# Revit family: 872-00-002-DN80-900
name_source: partatom
category: Pipe Accessories
units: mm (PartAtom-declared; Revit-internal decimal feet)

## family parameters
Always vertical = Yes
Cut with Voids When Loaded = No
Part Type = Valve - Breaks Into
Round Connector Dimension = Use Diameter
Shared = No
Work Plane-Based = No

## types (13) — shared parameters
Body_wallthickness = 10 mm  [stored 0.0328084 ft]
DN080_PN25 = 872-0080-00-70900100100
DN100_PN25 = 872-0100-00-70900100100
DN150_PN25 = 872-0150-00-70900100100
DN200_PN25 = 872-0200-00-70100100000
DN250_PN25 = 872-0250-00-70100100000
DN300_PN25 = 872-0300-00-70100100000
DN350_PN25 = 872-0350-00-70100100000
DN400_PN25 = 872-0400-00-70100100000
DN450_PN25 = 872-0450-00-70100100000
DN500_PN25 = 872-0500-00-70100100000
DN600_PN25 = 872-0600-00-70100100000
DN800_PN25 = 872-0800-00-70100100000
DN900_PN25 = 872-0900-00-70100100000
Description_ = AVK NEEDLE VALVE
RF_Thick = 3 mm  [stored 0.00984252 ft]
Search_Table = 872-00-002-DN80-900
URL product pages = https://www.avkvalves.com

## per-type parameters (varying)
- DN0080_PN25: (A_ref+W)/2=303 mm; A=125 mm; A_ref=275 mm; B=117 mm; D=100 mm; DN=80 mm  [stored 0.262467 ft]; FOD=95 mm; FOD_ref=50 mm  [stored 0.164042 ft]; FOD_ref_2=32 mm  [stored 0.104987 ft]; Fillet_thickness=10 mm  [stored 0.0328084 ft]; Flange_thickness=19 mm  [stored 0.062336 ft]; Flange_thickness_ref=10 mm  [stored 0.0328084 ft]; Flange_thickness_ref_2=5 mm  [stored 0.0164042 ft]; H3=230 mm; H3_ref=195 mm; ID=40 mm  [stored 0.131234 ft]; ID_ref=70 mm  [stored 0.229659 ft]; ID_ref_2=35 mm  [stored 0.114829 ft]; ID_ref_3=105 mm; ID_ref_4=35 mm  [stored 0.114829 ft]; L=260 mm; L1=111 mm; L2=65 mm  [stored 0.213255 ft]; Rf_Dia=66 mm  [stored 0.216535 ft]; Ring_Dia=35 mm  [stored 0.114829 ft]; Ring_Dia_2=15 mm  [stored 0.0492126 ft]; W=330 mm
- DN0100_PN25: (A_ref+W)/2=339 mm; A=145 mm; A_ref=308 mm; B=117 mm; D=120 mm; DN=100 mm; FOD=100 mm; FOD_ref=60 mm  [stored 0.19685 ft]; FOD_ref_2=33 mm; Fillet_thickness=10 mm  [stored 0.0328084 ft]; Flange_thickness=19 mm  [stored 0.062336 ft]; Flange_thickness_ref=10 mm  [stored 0.0328084 ft]; Flange_thickness_ref_2=5 mm  [stored 0.0164042 ft]; H3=235 mm; H3_ref=200 mm; ID=50 mm  [stored 0.164042 ft]; ID_ref=70 mm  [stored 0.229659 ft]; ID_ref_2=35 mm  [stored 0.114829 ft]; ID_ref_3=105 mm; ID_ref_4=35 mm  [stored 0.114829 ft]; L=300 mm; L1=131 mm; L2=75 mm  [stored 0.246063 ft]; Rf_Dia=78 mm  [stored 0.255906 ft]; Ring_Dia=35 mm  [stored 0.114829 ft]; Ring_Dia_2=15 mm  [stored 0.0492126 ft]; W=370 mm
- DN0150_PN25: (A_ref+W)/2=403 mm; A=175 mm; A_ref=370 mm; B=150 mm; D=135 mm; DN=150 mm; FOD=130 mm; FOD_ref=85 mm; FOD_ref_2=43 mm  [stored 0.141076 ft]; Fillet_thickness=10 mm  [stored 0.0328084 ft]; Flange_thickness=19 mm  [stored 0.062336 ft]; Flange_thickness_ref=10 mm  [stored 0.0328084 ft]; Flange_thickness_ref_2=5 mm  [stored 0.0164042 ft]; H3=300 mm; H3_ref=265 mm; ID=75 mm  [stored 0.246063 ft]; ID_ref=70 mm  [stored 0.229659 ft]; ID_ref_2=35 mm  [stored 0.114829 ft]; ID_ref_3=105 mm; ID_ref_4=35 mm  [stored 0.114829 ft]; L=350 mm; L1=156 mm; L2=88 mm; Rf_Dia=106 mm; Ring_Dia=35 mm  [stored 0.114829 ft]; Ring_Dia_2=15 mm  [stored 0.0492126 ft]; W=435 mm
- DN0200_PN25: (A_ref+W)/2=480 mm; A=220 mm; A_ref=450 mm; B=150 mm; D=150 mm; DN=200 mm; FOD=170 mm; FOD_ref=110 mm; FOD_ref_2=57 mm; Fillet_thickness=20 mm  [stored 0.0656168 ft]; Flange_thickness=20 mm  [stored 0.0656168 ft]; Flange_thickness_ref=10 mm  [stored 0.0328084 ft]; Flange_thickness_ref_2=5 mm  [stored 0.0164042 ft]; H3=425 mm; H3_ref=380 mm; ID=100 mm; ID_ref=90 mm; ID_ref_2=45 mm  [stored 0.147638 ft]; ID_ref_3=135 mm; ID_ref_4=45 mm  [stored 0.147638 ft]; L=400 mm; L1=180 mm; L2=100 mm; Rf_Dia=133 mm; Ring_Dia=45 mm  [stored 0.147638 ft]; Ring_Dia_2=25 mm  [stored 0.082021 ft]; W=510 mm
- DN0250_PN25: (A_ref+W)/2=550 mm; A=260 mm; A_ref=520 mm; B=150 mm; D=165 mm; DN=250 mm; FOD=200 mm; FOD_ref=135 mm; FOD_ref_2=67 mm; Fillet_thickness=22 mm  [stored 0.0721785 ft]; Flange_thickness=22 mm  [stored 0.0721785 ft]; Flange_thickness_ref=11 mm  [stored 0.0360892 ft]; Flange_thickness_ref_2=6 mm  [stored 0.019685 ft]; H3=475 mm; H3_ref=415 mm; ID=125 mm; ID_ref=120 mm; ID_ref_2=60 mm  [stored 0.19685 ft]; ID_ref_3=180 mm; ID_ref_4=60 mm  [stored 0.19685 ft]; L=450 mm; L1=203 mm; L2=113 mm; Rf_Dia=160 mm; Ring_Dia=60 mm  [stored 0.19685 ft]; Ring_Dia_2=40 mm  [stored 0.131234 ft]; W=580 mm
- DN0300_PN25: (A_ref+W)/2=654 mm; A=305 mm; A_ref=614 mm; B=284 mm; D=185 mm; DN=300 mm; FOD=228 mm; FOD_ref=160 mm; FOD_ref_2=76 mm; Fillet_thickness=25 mm  [stored 0.082021 ft]; Flange_thickness=25 mm  [stored 0.082021 ft]; Flange_thickness_ref=12 mm  [stored 0.0393701 ft]; Flange_thickness_ref_2=6 mm  [stored 0.019685 ft]; H3=535 mm; H3_ref=470 mm; ID=150 mm; ID_ref=130 mm; ID_ref_2=65 mm  [stored 0.213255 ft]; ID_ref_3=195 mm; ID_ref_4=65 mm  [stored 0.213255 ft]; L=500 mm; L1=226 mm; L2=125 mm; Rf_Dia=185 mm; Ring_Dia=65 mm  [stored 0.213255 ft]; Ring_Dia_2=45 mm  [stored 0.147638 ft]; W=695 mm
- DN0350_PN25: (A_ref+W)/2=729 mm; A=345 mm; A_ref=688 mm; B=300 mm; D=205 mm; DN=350 mm; FOD=260 mm; FOD_ref=185 mm; FOD_ref_2=87 mm; Fillet_thickness=27 mm; Flange_thickness=27 mm; Flange_thickness_ref=13 mm; Flange_thickness_ref_2=7 mm  [stored 0.0229659 ft]; H3=595 mm; H3_ref=520 mm; ID=175 mm; ID_ref=150 mm; ID_ref_2=75 mm  [stored 0.246063 ft]; ID_ref_3=225 mm; ID_ref_4=75 mm  [stored 0.246063 ft]; L=550 mm; L1=249 mm; L2=138 mm; Rf_Dia=215 mm; Ring_Dia=75 mm  [stored 0.246063 ft]; Ring_Dia_2=55 mm  [stored 0.180446 ft]; W=770 mm
- DN0400_PN25: (A_ref+W)/2=803 mm; A=385 mm; A_ref=760 mm; B=300 mm; D=235 mm; DN=400 mm; FOD=290 mm; FOD_ref=210 mm; FOD_ref_2=97 mm; Fillet_thickness=28 mm  [stored 0.0918635 ft]; Flange_thickness=28 mm  [stored 0.0918635 ft]; Flange_thickness_ref=14 mm  [stored 0.0459318 ft]; Flange_thickness_ref_2=7 mm  [stored 0.0229659 ft]; H3=660 mm; H3_ref=585 mm; ID=200 mm; ID_ref=150 mm; ID_ref_2=75 mm  [stored 0.246063 ft]; ID_ref_3=225 mm; ID_ref_4=75 mm  [stored 0.246063 ft]; L=600 mm; L1=272 mm; L2=150 mm; Rf_Dia=240 mm; Ring_Dia=75 mm  [stored 0.246063 ft]; Ring_Dia_2=55 mm  [stored 0.180446 ft]; W=845 mm
- DN0450_PN25: (A_ref+W)/2=859 mm; A=415 mm; A_ref=818 mm; B=305 mm; D=240 mm; DN=450 mm; FOD=320 mm; FOD_ref=235 mm; FOD_ref_2=107 mm; Fillet_thickness=30 mm  [stored 0.0984252 ft]; Flange_thickness=30 mm  [stored 0.0984252 ft]; Flange_thickness_ref=15 mm  [stored 0.0492126 ft]; Flange_thickness_ref_2=8 mm  [stored 0.0262467 ft]; H3=745 mm; H3_ref=670 mm; ID=225 mm; ID_ref=150 mm; ID_ref_2=75 mm  [stored 0.246063 ft]; ID_ref_3=225 mm; ID_ref_4=75 mm  [stored 0.246063 ft]; L=650 mm; L1=295 mm; L2=163 mm; Rf_Dia=274 mm; Ring_Dia=75 mm  [stored 0.246063 ft]; Ring_Dia_2=55 mm  [stored 0.180446 ft]; W=900 mm
- DN0500_PN25: (A_ref+W)/2=921 mm; A=445 mm; A_ref=881 mm; B=305 mm; D=245 mm; DN=500 mm; FOD=358 mm; FOD_ref=260 mm; FOD_ref_2=119 mm; Fillet_thickness=32 mm  [stored 0.104987 ft]; Flange_thickness=32 mm  [stored 0.104987 ft]; Flange_thickness_ref=16 mm; Flange_thickness_ref_2=8 mm  [stored 0.0262467 ft]; H3=785 mm; H3_ref=710 mm; ID=250 mm; ID_ref=150 mm; ID_ref_2=75 mm  [stored 0.246063 ft]; ID_ref_3=225 mm; ID_ref_4=75 mm  [stored 0.246063 ft]; L=700 mm; L1=319 mm; L2=175 mm; Rf_Dia=291 mm; Ring_Dia=75 mm  [stored 0.246063 ft]; Ring_Dia_2=55 mm  [stored 0.180446 ft]; W=960 mm
- DN0600_PN25: (A_ref+W)/2=1040 mm; A=505 mm; A_ref=1002 mm; B=305 mm; D=280 mm; DN=600 mm; FOD=420 mm; FOD_ref=310 mm; FOD_ref_2=140 mm; Fillet_thickness=36 mm  [stored 0.11811 ft]; Flange_thickness=36 mm  [stored 0.11811 ft]; Flange_thickness_ref=18 mm  [stored 0.0590551 ft]; Flange_thickness_ref_2=9 mm  [stored 0.0295276 ft]; H3=925 mm; H3_ref=845 mm; ID=300 mm; ID_ref=160 mm; ID_ref_2=80 mm  [stored 0.262467 ft]; ID_ref_3=240 mm; ID_ref_4=80 mm  [stored 0.262467 ft]; L=800 mm; L1=364 mm; L2=200 mm; Rf_Dia=360 mm; Ring_Dia=80 mm  [stored 0.262467 ft]; Ring_Dia_2=60 mm  [stored 0.19685 ft]; W=1078 mm
- DN0800_PN25: (A_ref+W)/2=1317 mm; A=650 mm; A_ref=1264 mm; B=510 mm; D=360 mm; DN=800 mm; FOD=508 mm; FOD_ref=410 mm; FOD_ref_2=169 mm; Fillet_thickness=40 mm  [stored 0.131234 ft]; Flange_thickness=40 mm  [stored 0.131234 ft]; Flange_thickness_ref=20 mm  [stored 0.0656168 ft]; Flange_thickness_ref_2=10 mm  [stored 0.0328084 ft]; H3=1180 mm; H3_ref=1100 mm; ID=400 mm; ID_ref=160 mm; ID_ref_2=80 mm  [stored 0.262467 ft]; ID_ref_3=240 mm; ID_ref_4=80 mm  [stored 0.262467 ft]; L=1000 mm; L1=460 mm; L2=250 mm; Rf_Dia=450 mm; Ring_Dia=80 mm  [stored 0.262467 ft]; Ring_Dia_2=60 mm  [stored 0.19685 ft]; W=1370 mm
- DN0900_PN25: (A_ref+W)/2=1466 mm; A=715 mm; A_ref=1401 mm; B=510 mm; D=385 mm; DN=900 mm; FOD=558 mm; FOD_ref=460 mm; FOD_ref_2=186 mm; Fillet_thickness=40 mm  [stored 0.131234 ft]; Flange_thickness=40 mm  [stored 0.131234 ft]; Flange_thickness_ref=20 mm  [stored 0.0656168 ft]; Flange_thickness_ref_2=10 mm  [stored 0.0328084 ft]; H3=1350 mm; H3_ref=1265 mm; ID=450 mm; ID_ref=170 mm; ID_ref_2=85 mm; ID_ref_3=255 mm; ID_ref_4=85 mm; L=1200 mm; L1=560 mm; L2=300 mm; Rf_Dia=500 mm; Ring_Dia=85 mm; Ring_Dia_2=65 mm  [stored 0.213255 ft]; W=1530 mm

note: [stored X ft] marks values corroborated as IEEE doubles in the binary element streams (Revit-internal decimal feet)

## geometry (parser evidence)
native form markers: Sweep x13
no freeform markers — native parametric forms only
